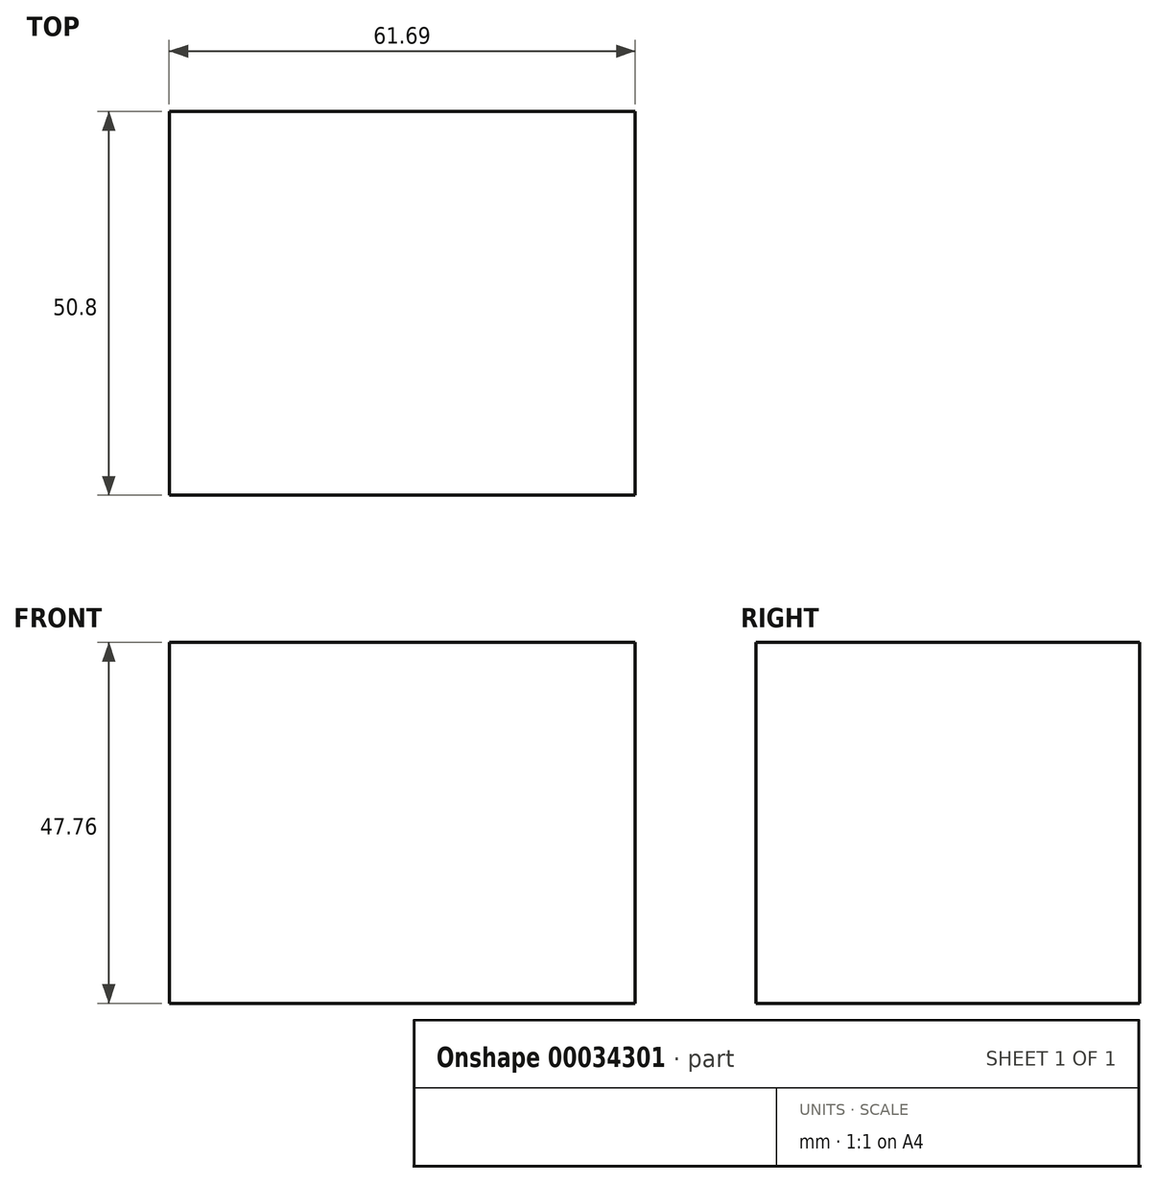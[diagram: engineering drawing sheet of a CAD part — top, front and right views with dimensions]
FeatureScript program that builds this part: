
annotation { "Feature Type Name" : "Feature", "Feature Type Description" : "" }
export const myFeature = defineFeature(function(context is Context, id is Id, definition is map)
    precondition{}
    {
        {
            var Q0;
            Q0=qCreatedBy(makeId("Front.planeOp"),FACE);
            var sketch = newSketch(context, id + "F0", { "sketchPlane" : qUnion([Q0])});
            skLineSegment(sketch, "E0.bottom", {"start": v(-114.2, 12.86) * mm, "end": v(-52.52, 12.86) * mm});
            skLineSegment(sketch, "E0.top", {"start": v(-114.2, 60.62) * mm, "end": v(-52.52, 60.62) * mm});
            skLineSegment(sketch, "E0.left", {"start": v(-114.2, 12.86) * mm, "end": v(-114.2, 60.62) * mm});
            skLineSegment(sketch, "E0.right", {"start": v(-52.52, 12.86) * mm, "end": v(-52.52, 60.62) * mm});
            skSolve(sketch);
        }
        {
            var Q0;
            Q0=makeQuery(id+"F0.imprint","IMPRINT",FACE,{"disambiguationData":[TD([[makeQuery(id+"F0.imprint","IMPRINT",EDGE,{"derivedFrom":sQuery(id+"F0.wireOp",EDGE,"E0.bottom")}),1.0]])]});
            extrude(context, id + "F1", {"entities" : qUnion([Q0]), "endBound" : BoundingType.SYMMETRIC, "depth" : 50.8 * mm});
        }
    });
